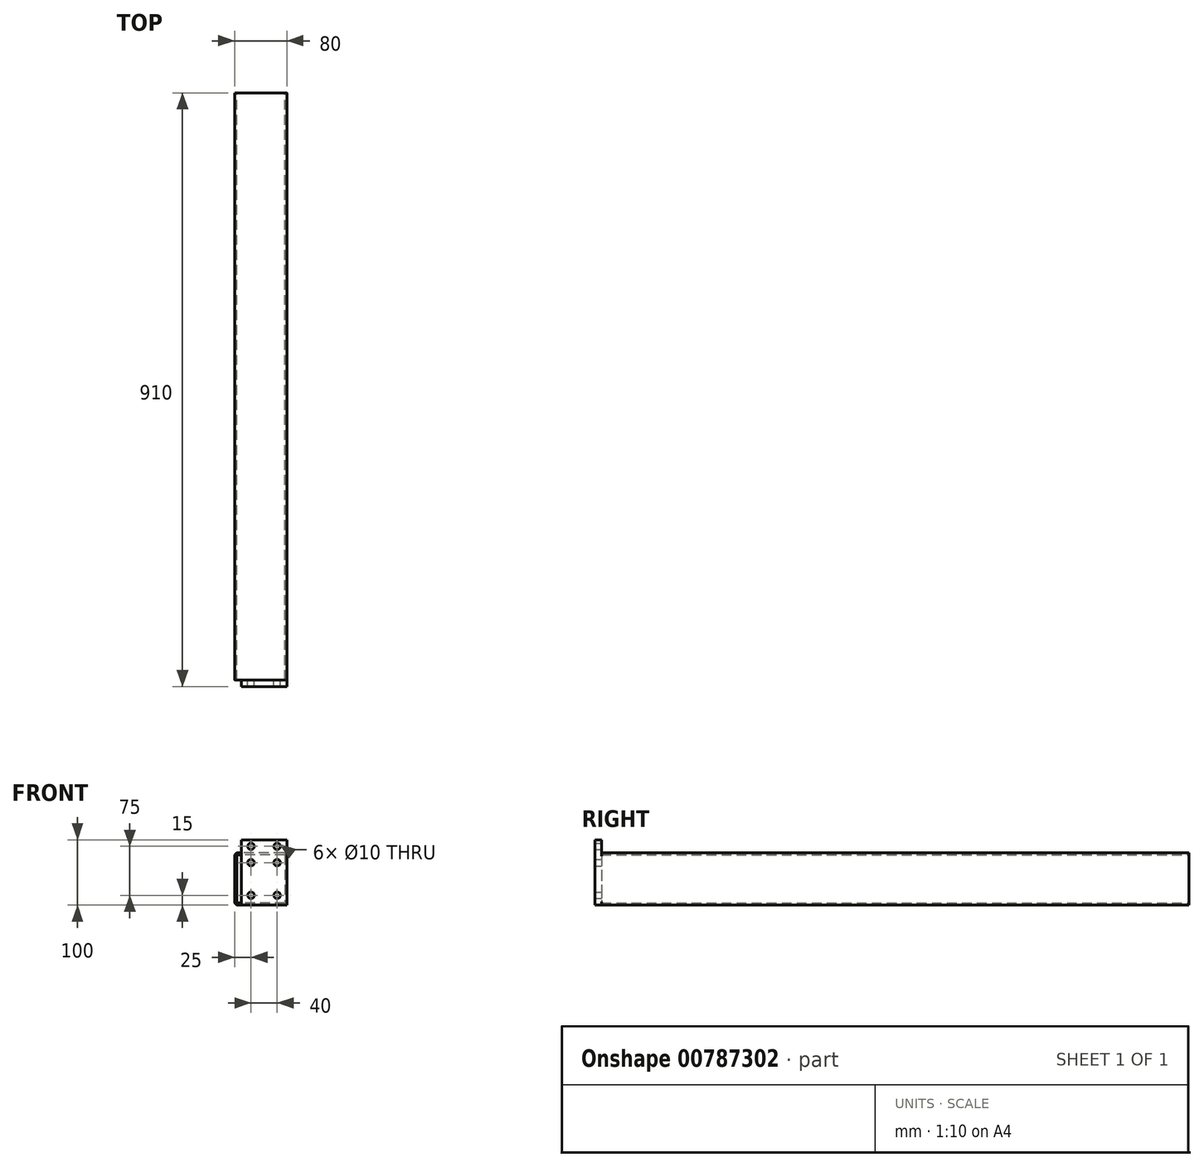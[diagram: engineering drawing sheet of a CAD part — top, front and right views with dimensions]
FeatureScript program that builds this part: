
annotation { "Feature Type Name" : "Feature", "Feature Type Description" : "" }
export const myFeature = defineFeature(function(context is Context, id is Id, definition is map)
    precondition{}
    {
        {
            var Q0;
            Q0=qCreatedBy(makeId("Front.planeOp"),FACE);
            var sketch = newSketch(context, id + "F0", { "sketchPlane" : qUnion([Q0])});
            skLineSegment(sketch, "E0.bottom", {"start": v(35, 40) * mm, "end": v(-35, 40) * mm});
            skLineSegment(sketch, "E0.top", {"start": v(35, -40) * mm, "end": v(-35, -40) * mm});
            skLineSegment(sketch, "E0.left", {"start": v(40, 35) * mm, "end": v(40, -35) * mm});
            skLineSegment(sketch, "E0.right", {"start": v(-40, 35) * mm, "end": v(-40, -35) * mm});
            skPoint(sketch, "E0.middle", {"position": v(0, 0) * mm});
            skPoint(sketch, "E1.visualSharp", {"position": v(-40, 40) * mm});
            skArc(sketch, "E1.filletArc", {"start": v(-35, 40) * mm, "mid": v(-38.54, 38.54) * mm, "end": v(-40, 35) * mm});
            skPoint(sketch, "E2.visualSharp", {"position": v(40, 40) * mm});
            skArc(sketch, "E2.filletArc", {"start": v(40, 35) * mm, "mid": v(38.54, 38.54) * mm, "end": v(35, 40) * mm});
            skPoint(sketch, "E3.visualSharp", {"position": v(40, -40) * mm});
            skArc(sketch, "E3.filletArc", {"start": v(35, -40) * mm, "mid": v(38.54, -38.54) * mm, "end": v(40, -35) * mm});
            skPoint(sketch, "E4.visualSharp", {"position": v(-40, -40) * mm});
            skArc(sketch, "E4.filletArc", {"start": v(-40, -35) * mm, "mid": v(-38.54, -38.54) * mm, "end": v(-35, -40) * mm});
            skLineSegment(sketch, "E5.0", {"start": v(-37, 37) * mm, "end": v(-37, -37) * mm});
            skLineSegment(sketch, "E5.1", {"start": v(37, 37) * mm, "end": v(-37, 37) * mm});
            skLineSegment(sketch, "E5.2", {"start": v(37, 37) * mm, "end": v(37, -37) * mm});
            skLineSegment(sketch, "E5.3", {"start": v(37, -37) * mm, "end": v(-37, -37) * mm});
            skSolve(sketch);
        }
        {
            var Q0;
            Q0=makeQuery(id+"F0.imprint","IMPRINT",FACE,{"disambiguationData":[TD([[makeQuery(id+"F0.imprint","IMPRINT",EDGE,{"derivedFrom":sQuery(id+"F0.wireOp",EDGE,"E0.bottom")}),1.0]])]});
            extrude(context, id + "F1", {"entities" : qUnion([Q0]), "depth" : 900 * mm, "offsetDistance" : 25 * mm});
        }
        {
            var Q0;
            Q0=makeQuery(id+"F1.opExtrude","CAP_FACE",FACE,{"disambiguationData":[OSD([sQuery(id+"F0.wireOp",EDGE,"E0.bottom"),sQuery(id+"F0.wireOp",EDGE,"E0.top"),sQuery(id+"F0.wireOp",EDGE,"E0.left"),sQuery(id+"F0.wireOp",EDGE,"E0.right"),sQuery(id+"F0.wireOp",EDGE,"E1.filletArc"),sQuery(id+"F0.wireOp",EDGE,"E2.filletArc"),sQuery(id+"F0.wireOp",EDGE,"E3.filletArc"),sQuery(id+"F0.wireOp",EDGE,"E4.filletArc"),sQuery(id+"F0.wireOp",EDGE,"E5.0"),sQuery(id+"F0.wireOp",EDGE,"E5.1"),sQuery(id+"F0.wireOp",EDGE,"E5.2"),sQuery(id+"F0.wireOp",EDGE,"E5.3")])],"isStart":false});
            var sketch = newSketch(context, id + "F2", { "sketchPlane" : qUnion([Q0])});
            skLineSegment(sketch, "E6.top", {"start": v(-30, -40) * mm, "end": v(40, -40) * mm});
            skLineSegment(sketch, "E6.right", {"start": v(40, 60) * mm, "end": v(40, -40) * mm});
            skLineSegment(sketch, "E7.right", {"start": v(-30, -40) * mm, "end": v(-30, 60) * mm});
            skLineSegment(sketch, "E8.top", {"start": v(40, 60) * mm, "end": v(-30, 60) * mm});
            skLineSegment(sketch, "E8.left", {"start": v(40, 60) * mm, "end": v(40, 60) * mm});
            skPoint(sketch, "E6.bottom.start.orphan", {"position": v(-40, 40) * mm});
            skPoint(sketch, "E9.orphan", {"position": v(-40, 60) * mm});
            skSolve(sketch);
        }
        {
            var Q0;
            {var subQ5=makeQuery(id+"F1.opExtrude","CAP_EDGE",EDGE,{"disambiguationData":[OSD([sQuery(id+"F0.wireOp",EDGE,"E5.2")])],"isStart":false});Q0=makeQuery(id+"F2.imprint","IMPRINT",FACE,{"disambiguationData":[TD([[makeQuery(id+"F2.imprint","IMPRINT",EDGE,{"derivedFrom":subQ5}),-1.0]])]});}
            var Q1;
            {var subQ2=sQuery(id+"F2.wireOp",EDGE,"E6.top");Q1=makeQuery(id+"F2.imprint","IMPRINT",FACE,{"disambiguationData":[TD([[makeQuery(id+"F2.imprint","IMPRINT",EDGE,{"derivedFrom":subQ2}),1.0]])]});}
            var Q2;
            {var subQ6=makeQuery(id+"F1.opExtrude","CAP_EDGE",EDGE,{"disambiguationData":[OSD([sQuery(id+"F0.wireOp",EDGE,"E2.filletArc")])],"isStart":false});Q2=makeQuery(id+"F2.imprint","IMPRINT",FACE,{"disambiguationData":[TD([[makeQuery(id+"F2.imprint","IMPRINT",EDGE,{"derivedFrom":subQ6}),1.0]])]});}
            var Q3;
            {var subQ0=sQuery(id+"F2.wireOp",EDGE,"E8.top");Q3=makeQuery(id+"F2.imprint","IMPRINT",FACE,{"disambiguationData":[TD([[makeQuery(id+"F2.imprint","IMPRINT",EDGE,{"derivedFrom":subQ0}),1.0]])]});}
            extrude(context, id + "F3", {"entities" : qUnion([Q0, Q1, Q2, Q3]), "operationType" : NewBodyOperationType.ADD, "depth" : 10 * mm, "offsetDistance" : 25 * mm});
        }
        {
            var Q0;
            {var subQ2=sQuery(id+"F0.wireOp",EDGE,"E5.1");var subQ3=sQuery(id+"F0.wireOp",EDGE,"E2.filletArc");var subQ4=sQuery(id+"F2.wireOp",EDGE,"E7.right");Q0=makeQuery(id+"F3.boolean.opBoolean","SPLIT",FACE,{"disambiguationData":[TD([makeQuery(id+"F1.opExtrude","SWEPT_FACE",FACE,{"disambiguationData":[OSD([subQ2])]})])],"derivedFrom":makeQuery(id+"F3.opExtrude","CAP_FACE",FACE,{"disambiguationData":[OSD([subQ3,sQuery(id+"F2.wireOp",EDGE,"E6.bottom"),sQuery(id+"F2.wireOp",EDGE,"E6.top"),sQuery(id+"F2.wireOp",EDGE,"E6.right"),subQ4])],"isStart":true})});}
            var sketch = newSketch(context, id + "F4", { "sketchPlane" : qUnion([Q0])});
            skCircle(sketch, "E10", {"center": v(-25, 50) * mm, "radius": 5 * mm});
            skCircle(sketch, "E11", {"center": v(15, 50) * mm, "radius": 5 * mm});
            skCircle(sketch, "E12", {"center": v(15, 25) * mm, "radius": 5 * mm});
            skCircle(sketch, "E13", {"center": v(-25, 25) * mm, "radius": 5 * mm});
            skCircle(sketch, "E14", {"center": v(-25, -25) * mm, "radius": 5 * mm});
            skCircle(sketch, "E15", {"center": v(15, -25) * mm, "radius": 5 * mm});
            skSolve(sketch);
        }
        {
            var Q0;
            Q0 = qSketchRegion(id + "F4", true);
            extrude(context, id + "F5", {"entities" : qUnion([Q0]), "operationType" : NewBodyOperationType.REMOVE, "oppositeDirection" : true, "depth" : 25 * mm, "offsetDistance" : 25 * mm});
        }
        {
            var Q0;
            Q0=makeQuery(id+"F1.opExtrude","CAP_FACE",FACE,{"disambiguationData":[OSD([sQuery(id+"F0.wireOp",EDGE,"E0.bottom"),sQuery(id+"F0.wireOp",EDGE,"E0.top"),sQuery(id+"F0.wireOp",EDGE,"E0.left"),sQuery(id+"F0.wireOp",EDGE,"E0.right"),sQuery(id+"F0.wireOp",EDGE,"E1.filletArc"),sQuery(id+"F0.wireOp",EDGE,"E2.filletArc"),sQuery(id+"F0.wireOp",EDGE,"E3.filletArc"),sQuery(id+"F0.wireOp",EDGE,"E4.filletArc"),sQuery(id+"F0.wireOp",EDGE,"E5.0"),sQuery(id+"F0.wireOp",EDGE,"E5.1"),sQuery(id+"F0.wireOp",EDGE,"E5.2"),sQuery(id+"F0.wireOp",EDGE,"E5.3")])],"isStart":false});
            var Q1;
            Q1=makeQuery(id+"F1.opExtrude","CAP_FACE",FACE,{"disambiguationData":[OSD([sQuery(id+"F0.wireOp",EDGE,"E0.bottom"),sQuery(id+"F0.wireOp",EDGE,"E0.top"),sQuery(id+"F0.wireOp",EDGE,"E0.left"),sQuery(id+"F0.wireOp",EDGE,"E0.right"),sQuery(id+"F0.wireOp",EDGE,"E1.filletArc"),sQuery(id+"F0.wireOp",EDGE,"E2.filletArc"),sQuery(id+"F0.wireOp",EDGE,"E3.filletArc"),sQuery(id+"F0.wireOp",EDGE,"E4.filletArc"),sQuery(id+"F0.wireOp",EDGE,"E5.0"),sQuery(id+"F0.wireOp",EDGE,"E5.1"),sQuery(id+"F0.wireOp",EDGE,"E5.2"),sQuery(id+"F0.wireOp",EDGE,"E5.3")])],"isStart":true});
            cPlane(context, id + "F6", {"entities" : qUnion([Q0, Q1]), "cplaneType" : CPlaneType.MID_PLANE, "offset" : 25 * mm, "width" : 150 * mm, "height" : 150 * mm});
        }
    });
